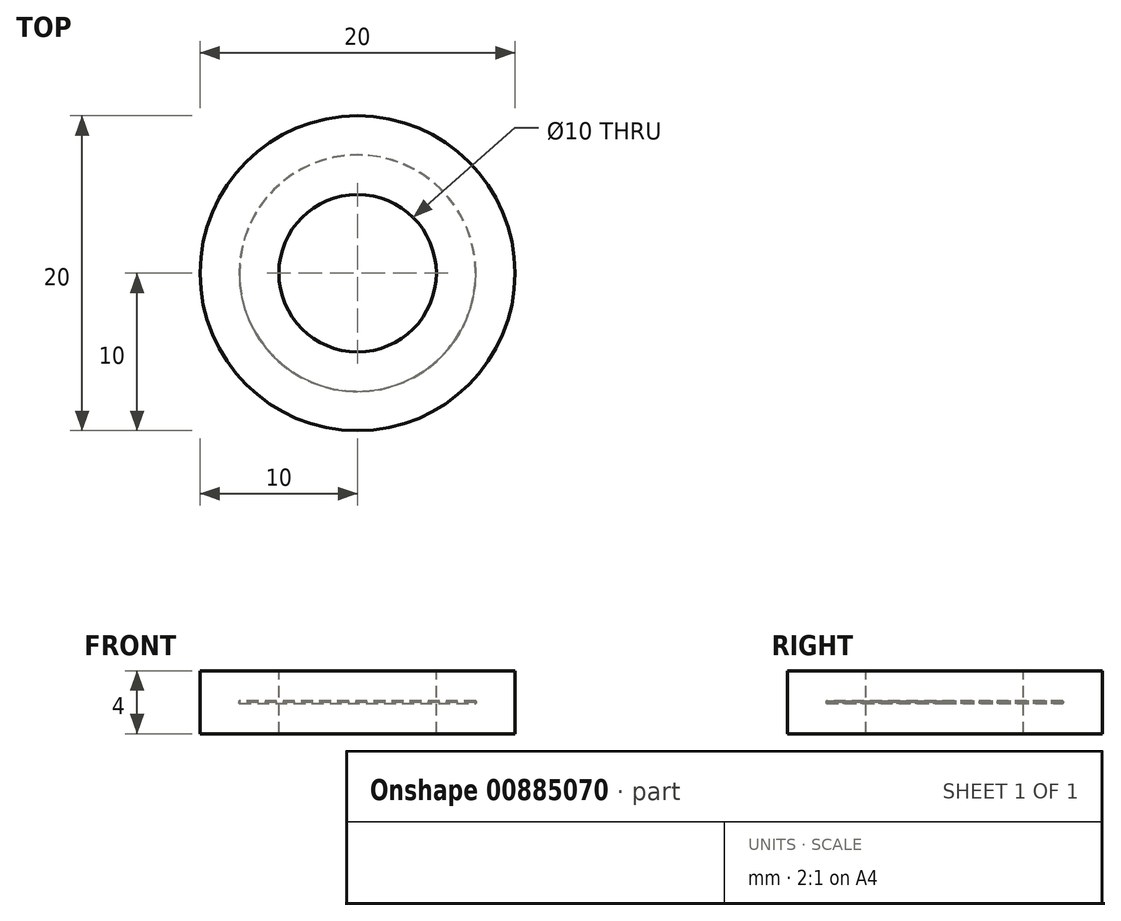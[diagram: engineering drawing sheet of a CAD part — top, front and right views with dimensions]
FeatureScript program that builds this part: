
annotation { "Feature Type Name" : "Feature", "Feature Type Description" : "" }
export const myFeature = defineFeature(function(context is Context, id is Id, definition is map)
    precondition{}
    {
        {
            var Q0;
            Q0=qCreatedBy(makeId("Top.planeOp"),FACE);
            var sketch = newSketch(context, id + "F0", { "sketchPlane" : qUnion([Q0])});
            skCircle(sketch, "E0", {"center": v(0, 0) * mm, "radius": 5 * mm});
            skCircle(sketch, "E1", {"center": v(0, 0) * mm, "radius": 7.53 * mm});
            skCircle(sketch, "E2", {"center": v(0, 0) * mm, "radius": 10 * mm});
            skCircle(sketch, "E3", {"center": v(0, 0) * mm, "radius": 7.5 * mm});
            skSolve(sketch);
        }
        {
            var Q0;
            Q0=makeQuery(id+"F0.imprint","IMPRINT",FACE,{"disambiguationData":[TD([[makeQuery(id+"F0.imprint","IMPRINT",EDGE,{"derivedFrom":sQuery(id+"F0.wireOp",EDGE,"E1")}),-1.0]])]});
            extrude(context, id + "F1", {"entities" : qUnion([Q0]), "depth" : 2 * mm, "offsetDistance" : 25.4 * mm, "hasDraft" : true, "draftAngle" : 10 * degree, "hasSecondDirection" : true, "secondDirectionOppositeDirection" : true, "secondDirectionDepth" : 2 * mm, "hasSecondDirectionDraft" : true, "secondDirectionDraftAngle" : 10 * degree});
        }
        {
            var Q0;
            Q0=makeQuery(id+"F0.imprint","IMPRINT",FACE,{"disambiguationData":[TD([[makeQuery(id+"F0.imprint","IMPRINT",EDGE,{"derivedFrom":sQuery(id+"F0.wireOp",EDGE,"E0")}),-1.0]])]});
            extrude(context, id + "F2", {"entities" : qUnion([Q0]), "operationType" : NewBodyOperationType.ADD, "depth" : 2 * mm, "offsetDistance" : 25.4 * mm, "hasDraft" : true, "draftAngle" : 10 * degree, "hasSecondDirection" : true, "secondDirectionOppositeDirection" : true, "secondDirectionDepth" : 2 * mm, "hasSecondDirectionDraft" : true, "secondDirectionDraftAngle" : 10 * degree});
        }
        {
            var Q0;
            Q0=qCreatedBy(makeId("Top.planeOp"),FACE);
            var sketch = newSketch(context, id + "F3", { "sketchPlane" : qUnion([Q0])});
            skCircle(sketch, "E4", {"center": v(0, 0) * mm, "radius": 10 * mm});
            skCircle(sketch, "E5", {"center": v(0, 0) * mm, "radius": 12.68 * mm});
            skSolve(sketch);
        }
        {
            var Q0;
            Q0=makeQuery(id+"F3.imprint","IMPRINT",FACE,{"disambiguationData":[TD([[makeQuery(id+"F3.imprint","IMPRINT",EDGE,{"derivedFrom":sQuery(id+"F3.wireOp",EDGE,"E4")}),-1.0]])]});
            extrude(context, id + "F4", {"entities" : qUnion([Q0]), "operationType" : NewBodyOperationType.REMOVE, "oppositeDirection" : true, "depth" : 2 * mm, "offsetDistance" : 25.4 * mm, "hasSecondDirection" : true, "secondDirectionOppositeDirection" : false, "secondDirectionDepth" : 2 * mm});
        }
        {
            var Q0;
            Q0=qCreatedBy(makeId("Top.planeOp"),FACE);
            var sketch = newSketch(context, id + "F5", { "sketchPlane" : qUnion([Q0])});
            skCircle(sketch, "E6", {"center": v(0, 0) * mm, "radius": 5 * mm});
            skCircle(sketch, "E7", {"center": v(0, 0) * mm, "radius": 1.88 * mm});
            skSolve(sketch);
        }
        {
            var Q0;
            Q0 = qSketchRegion(id + "F5", true);
            extrude(context, id + "F6", {"entities" : qUnion([Q0]), "operationType" : NewBodyOperationType.REMOVE, "oppositeDirection" : true, "depth" : 2 * mm, "offsetDistance" : 25.4 * mm, "hasSecondDirection" : true, "secondDirectionOppositeDirection" : false, "secondDirectionDepth" : 2 * mm});
        }
    });
